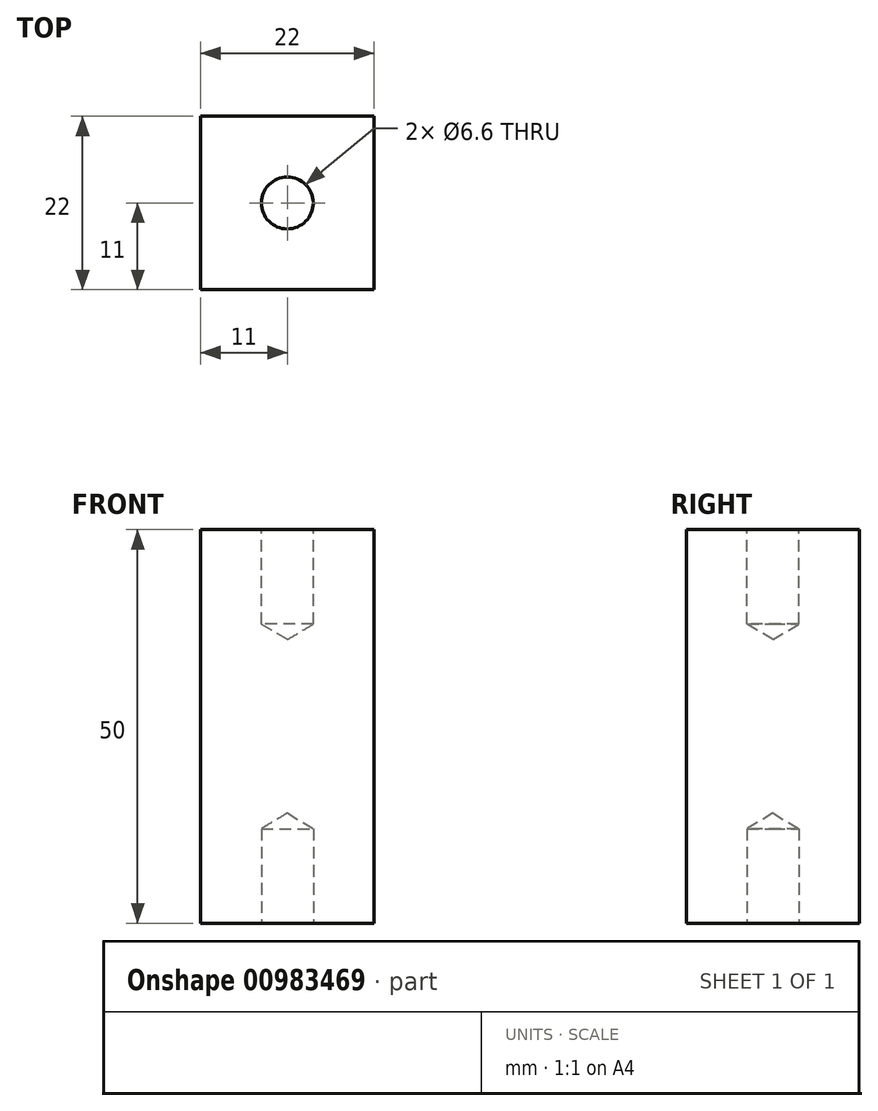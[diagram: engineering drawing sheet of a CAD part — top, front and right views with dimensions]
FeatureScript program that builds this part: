
annotation { "Feature Type Name" : "Feature", "Feature Type Description" : "" }
export const myFeature = defineFeature(function(context is Context, id is Id, definition is map)
    precondition{}
    {
        {
            var Q0;
            Q0=qCreatedBy(makeId("Top.planeOp"),FACE);
            var sketch = newSketch(context, id + "F0", { "sketchPlane" : qUnion([Q0])});
            skLineSegment(sketch, "E0.bottom", {"start": v(11, 11) * mm, "end": v(-11, 11) * mm});
            skLineSegment(sketch, "E0.top", {"start": v(11, -11) * mm, "end": v(-11, -11) * mm});
            skLineSegment(sketch, "E0.left", {"start": v(11, 11) * mm, "end": v(11, -11) * mm});
            skLineSegment(sketch, "E0.right", {"start": v(-11, 11) * mm, "end": v(-11, -11) * mm});
            skPoint(sketch, "E0.middle", {"position": v(0, 0) * mm});
            skSolve(sketch);
        }
        {
            var Q0;
            Q0 = qSketchRegion(id + "F0", true);
            extrude(context, id + "F1", {"entities" : qUnion([Q0]), "depth" : 50 * mm, "offsetDistance" : 25 * mm});
        }
        {
            var Q0;
            Q0=makeQuery(id+"F1.opExtrude","CAP_FACE",FACE,{"disambiguationData":[OSD([sQuery(id+"F0.wireOp",EDGE,"E0.bottom"),sQuery(id+"F0.wireOp",EDGE,"E0.top"),sQuery(id+"F0.wireOp",EDGE,"E0.left"),sQuery(id+"F0.wireOp",EDGE,"E0.right")])],"isStart":false});
            var sketch = newSketch(context, id + "F2", { "sketchPlane" : qUnion([Q0])});
            skPoint(sketch, "E1", {"position": v(0, 0) * mm});
            skSolve(sketch);
        }
        {
            var Q0;
            Q0=sQuery(id+"F2.wireOp",VERTEX,"E1");
            var Q1;
            Q1=makeQuery(id+"F1.opExtrude","SWEPT_BODY",BODY,{"disambiguationData":[OSD([sQuery(id+"F0.wireOp",EDGE,"E0.bottom"),sQuery(id+"F0.wireOp",EDGE,"E0.top"),sQuery(id+"F0.wireOp",EDGE,"E0.left"),sQuery(id+"F0.wireOp",EDGE,"E0.right")])]});
            hole(context, id + "F3", {"style" : HoleStyle.SIMPLE, "endStyle" : HoleEndStyle.BLIND, "standardTappedOrClearance" : lookupTablePath({ "fit" : "Normal", "standard" : "ISO", "size" : "M6", "type" : "Clearance" }), "standardBlindInLast" : lookupTablePath({ "fit" : "Normal", "standard" : "ISO", "engagement" : "75%", "pitch" : "1 mm", "size" : "M6", "type" : "Clearance & tapped" }), "holeDiameter" : 6.6 * mm, "majorDiameter" : 5 * mm, "holeDepth" : 12 * mm, "isTappedThrough" : true, "tappedDepth" : 12 * mm, "tapClearance" : 3, "locations" : qUnion([Q0]), "scope" : qUnion([Q1])});
        }
        {
            var Q0;
            Q0=makeQuery(id+"F1.opExtrude","CAP_FACE",FACE,{"disambiguationData":[OSD([sQuery(id+"F0.wireOp",EDGE,"E0.bottom"),sQuery(id+"F0.wireOp",EDGE,"E0.top"),sQuery(id+"F0.wireOp",EDGE,"E0.left"),sQuery(id+"F0.wireOp",EDGE,"E0.right")])],"isStart":true});
            var sketch = newSketch(context, id + "F4", { "sketchPlane" : qUnion([Q0])});
            skPoint(sketch, "E2", {"position": v(0, 0) * mm});
            skSolve(sketch);
        }
        {
            var Q0;
            Q0=sQuery(id+"F4.wireOp",VERTEX,"E2");
            var Q1;
            Q1=makeQuery(id+"F1.opExtrude","SWEPT_BODY",BODY,{"disambiguationData":[OSD([sQuery(id+"F0.wireOp",EDGE,"E0.bottom"),sQuery(id+"F0.wireOp",EDGE,"E0.top"),sQuery(id+"F0.wireOp",EDGE,"E0.left"),sQuery(id+"F0.wireOp",EDGE,"E0.right")])]});
            hole(context, id + "F5", {"style" : HoleStyle.SIMPLE, "endStyle" : HoleEndStyle.BLIND, "standardTappedOrClearance" : lookupTablePath({ "fit" : "Normal", "standard" : "ISO", "size" : "M6", "type" : "Clearance" }), "standardBlindInLast" : lookupTablePath({ "fit" : "Normal", "standard" : "ISO", "engagement" : "75%", "pitch" : "1 mm", "size" : "M6", "type" : "Clearance & tapped" }), "holeDiameter" : 6.6 * mm, "majorDiameter" : 5 * mm, "holeDepth" : 12 * mm, "isTappedThrough" : true, "tappedDepth" : 12 * mm, "tapClearance" : 3, "locations" : qUnion([Q0]), "scope" : qUnion([Q1])});
        }
    });
